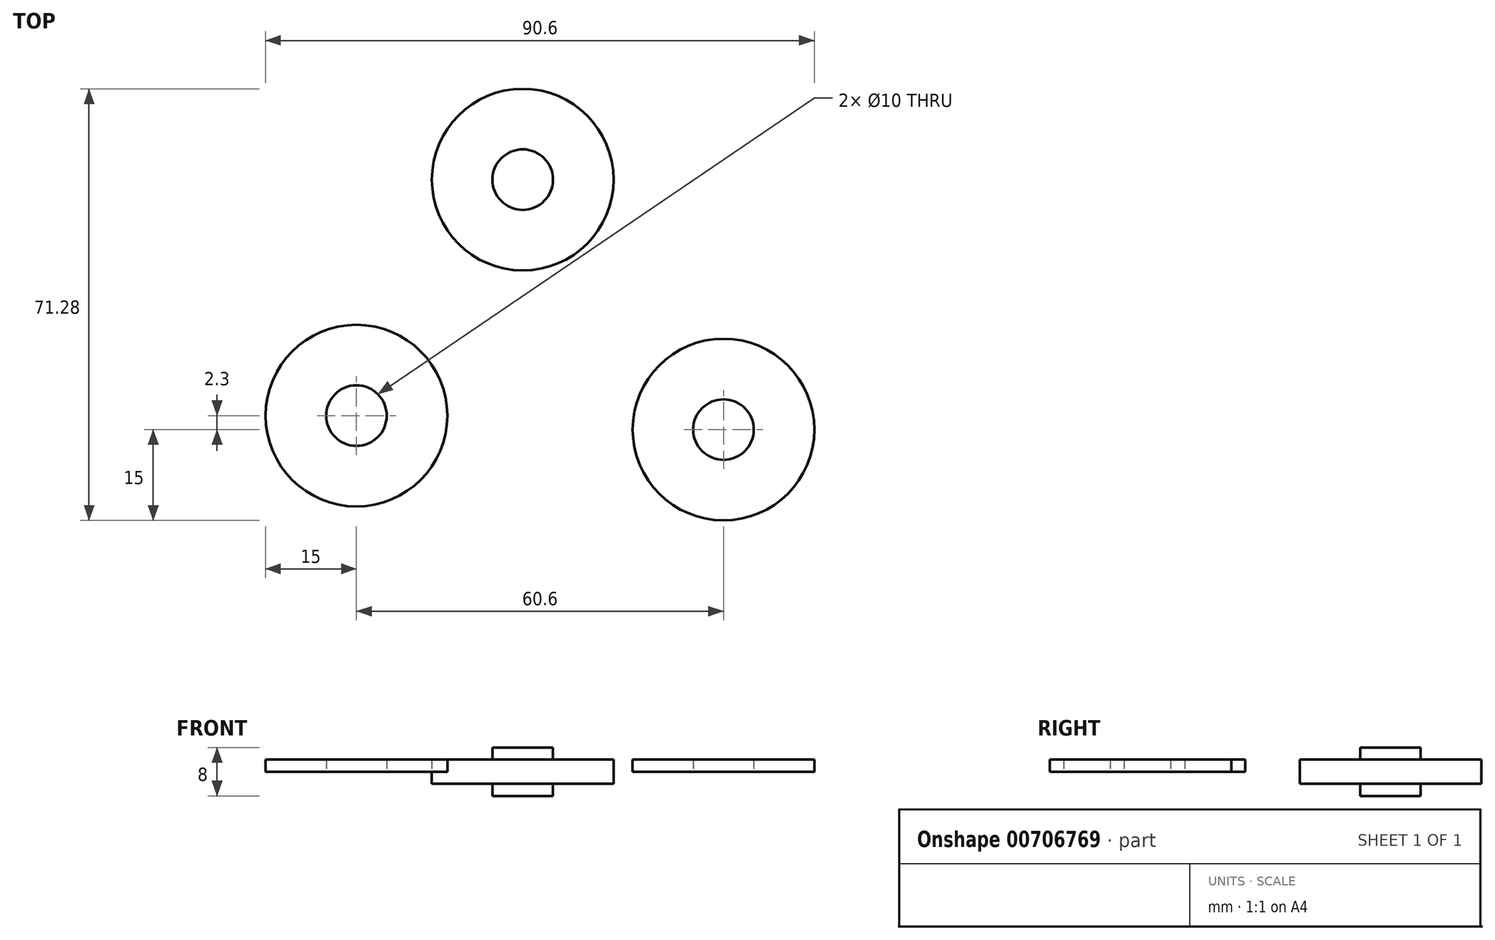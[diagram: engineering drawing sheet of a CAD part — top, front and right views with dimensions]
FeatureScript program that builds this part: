
annotation { "Feature Type Name" : "Feature", "Feature Type Description" : "" }
export const myFeature = defineFeature(function(context is Context, id is Id, definition is map)
    precondition{}
    {
        {
            var Q0;
            Q0=qCreatedBy(makeId("Top.planeOp"),FACE);
            var sketch = newSketch(context, id + "F0", { "sketchPlane" : qUnion([Q0])});
            skCircle(sketch, "E0", {"center": v(0, 0) * mm, "radius": 15 * mm});
            skCircle(sketch, "E1", {"center": v(0, 0) * mm, "radius": 5 * mm});
            skSolve(sketch);
        }
        {
            var Q0;
            Q0 = qSketchRegion(id + "F0", true);
            extrude(context, id + "F1", {"entities" : qUnion([Q0]), "depth" : 2 * mm, "offsetDistance" : 25 * mm});
        }
        {
            var Q0;
            Q0=makeQuery(id+"F1.opExtrude","SWEPT_BODY",BODY,{"disambiguationData":[OSD([sQuery(id+"F0.wireOp",EDGE,"E0"),sQuery(id+"F0.wireOp",EDGE,"E1")])]});
            transform(context, id + "F2", {"entities" : qUnion([Q0]), "transformType" : TransformType.TRANSLATION_3D, "dx" : -60.6 * mm, "dy" : 2.3 * mm, "dz" : 0 * mm, "makeCopy" : true});
        }
        {
            var Q0;
            Q0=qCreatedBy(makeId("Top.planeOp"),FACE);
            var sketch = newSketch(context, id + "F3", { "sketchPlane" : qUnion([Q0])});
            skCircle(sketch, "E2", {"center": v(-33.15, 41.28) * mm, "radius": 15 * mm});
            skSolve(sketch);
        }
        {
            var Q0;
            Q0 = qSketchRegion(id + "F3", true);
            extrude(context, id + "F4", {"entities" : qUnion([Q0]), "depth" : 2 * mm, "offsetDistance" : 25 * mm, "hasSecondDirection" : true, "secondDirectionOppositeDirection" : true, "secondDirectionDepth" : 2 * mm});
        }
        {
            var Q0;
            Q0=makeQuery(id+"F4.opExtrude","CAP_FACE",FACE,{"disambiguationData":[OSD([sQuery(id+"F3.wireOp",EDGE,"E2")])],"isStart":false});
            var sketch = newSketch(context, id + "F5", { "sketchPlane" : qUnion([Q0])});
            skCircle(sketch, "E3", {"center": v(-33.15, 41.28) * mm, "radius": 5 * mm});
            skSolve(sketch);
        }
        {
            var Q0;
            Q0 = qSketchRegion(id + "F5", true);
            extrude(context, id + "F6", {"entities" : qUnion([Q0]), "operationType" : NewBodyOperationType.ADD, "depth" : 2 * mm, "offsetDistance" : 25 * mm, "hasSecondDirection" : true, "secondDirectionOppositeDirection" : true, "secondDirectionDepth" : 6 * mm});
        }
    });
